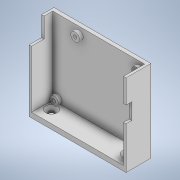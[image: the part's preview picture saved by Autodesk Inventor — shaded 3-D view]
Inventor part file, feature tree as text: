
AUTODESK INVENTOR PART (.ipt)
format: ipt  version: 2021 (Build 250183000, 183)  size: 202,240 bytes
history: native  units: mm
features: extrude x6, sketch x5, projected_geometry x3, chamfer x1
ambient origin geometry x8: Origin, YZ Plane, XZ Plane, XY Plane, X Axis, Y Axis, Z Axis, Center Point
bodies: Solid1 (feature_tree)
feature tree (15):
  extrude  "Extrusion1"  Depth=66.0mm
  sketch  "Sketch2"  dims[d2=3.0mm d3=0.0mm d4=4.0mm]
  extrude  "Extrusion2"  Depth=4.0mm
  extrude  "Extrusion3"  Depth=66.0mm
  extrude  "Extrusion4"  Depth=6.0mm
  chamfer  "Chamfer1"  Distance=2.8mm
  extrude  "Extrusion5"  Depth=7.0mm
  extrude  "Extrusion6"  Depth=3.0mm TaperAngle=0.0deg
  sketch  "Sketch1"  dims[d0=78.0mm d1=66.0mm]
  sketch  "Sketch3"  dims[d5=49.0mm d6=66.0mm]
  sketch  "Sketch4"  dims[d7=53.0mm d8=6.0mm]
  projected_geometry  "Projected Loop1"
  projected_geometry  "Projected Loop2"
  sketch  "Sketch5"  dims[d9=6.0mm d11=2.8mm d12=7.0mm d13=3.0mm d14=0.0mm d15=17.0mm d16=0.0mm d17=8.0mm d18=8.0mm d19=4.5mm d20=0.0mm d21=0.0mm d22=2.0mm d23=2.0mm d24=2.5mm d25=2.0mm d26=45.0deg d27=3.0mm d29=13.0mm d30=9.4mm d31=17.0mm d32=0.0mm d33=10.0mm d34=4.0mm d35=17.0mm d36=0.0mm d37=13.0mm]
  projected_geometry  "Projected Loop3"
